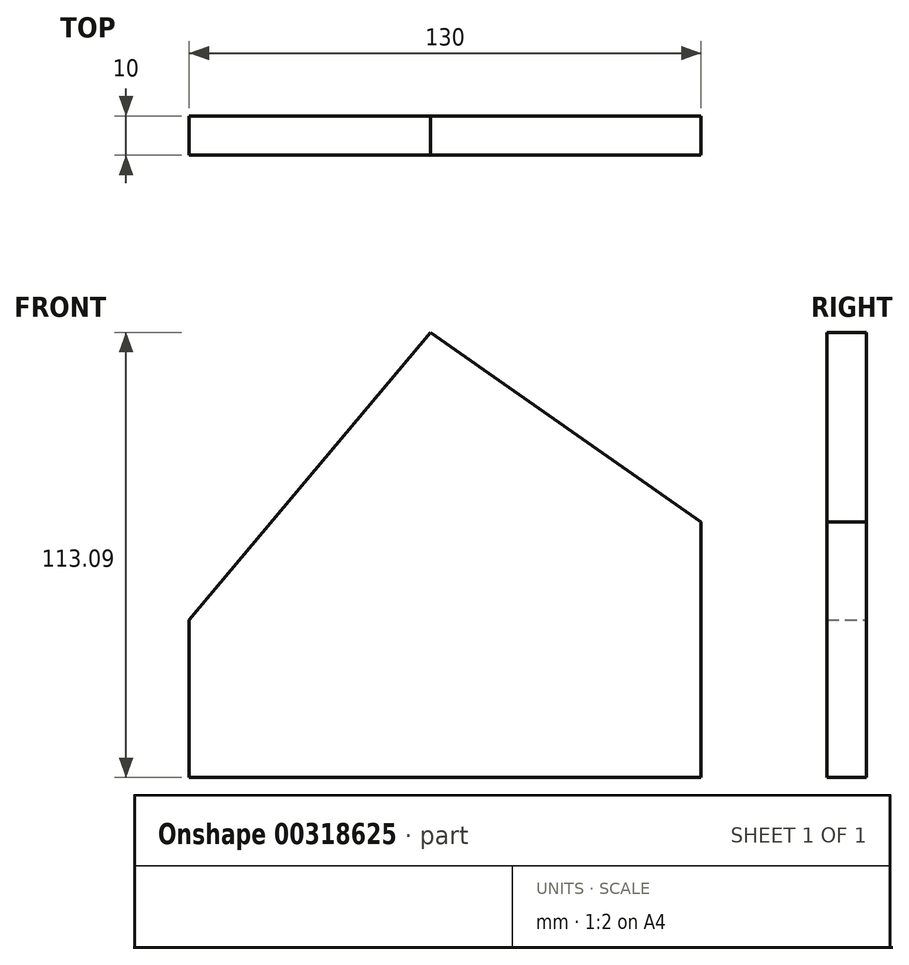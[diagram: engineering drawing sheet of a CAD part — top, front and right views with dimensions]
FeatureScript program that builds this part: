
annotation { "Feature Type Name" : "Feature", "Feature Type Description" : "" }
export const myFeature = defineFeature(function(context is Context, id is Id, definition is map)
    precondition{}
    {
        {
            var Q0;
            Q0=qCreatedBy(makeId("Front.planeOp"),FACE);
            var sketch = newSketch(context, id + "F0", { "sketchPlane" : qUnion([Q0])});
            skLineSegment(sketch, "E0", {"start": v(0, 0) * mm, "end": v(-130, 0) * mm});
            skLineSegment(sketch, "E1", {"start": v(-130, 0) * mm, "end": v(-130, 40) * mm});
            skLineSegment(sketch, "E2", {"start": v(-130, 40) * mm, "end": v(-68.67, 113.09) * mm});
            skLineSegment(sketch, "E3", {"start": v(-68.67, 113.09) * mm, "end": v(0, 65) * mm});
            skLineSegment(sketch, "E4", {"start": v(0, 65) * mm, "end": v(0, 0) * mm});
            skSolve(sketch);
        }
        {
            var Q0;
            Q0=makeQuery(id+"F0.imprint","IMPRINT",FACE,{"disambiguationData":[TD([[makeQuery(id+"F0.imprint","IMPRINT",EDGE,{"derivedFrom":sQuery(id+"F0.wireOp",EDGE,"E0")}),-1.0]])]});
            extrude(context, id + "F1", {"entities" : qUnion([Q0]), "depth" : 10 * mm});
        }
    });
